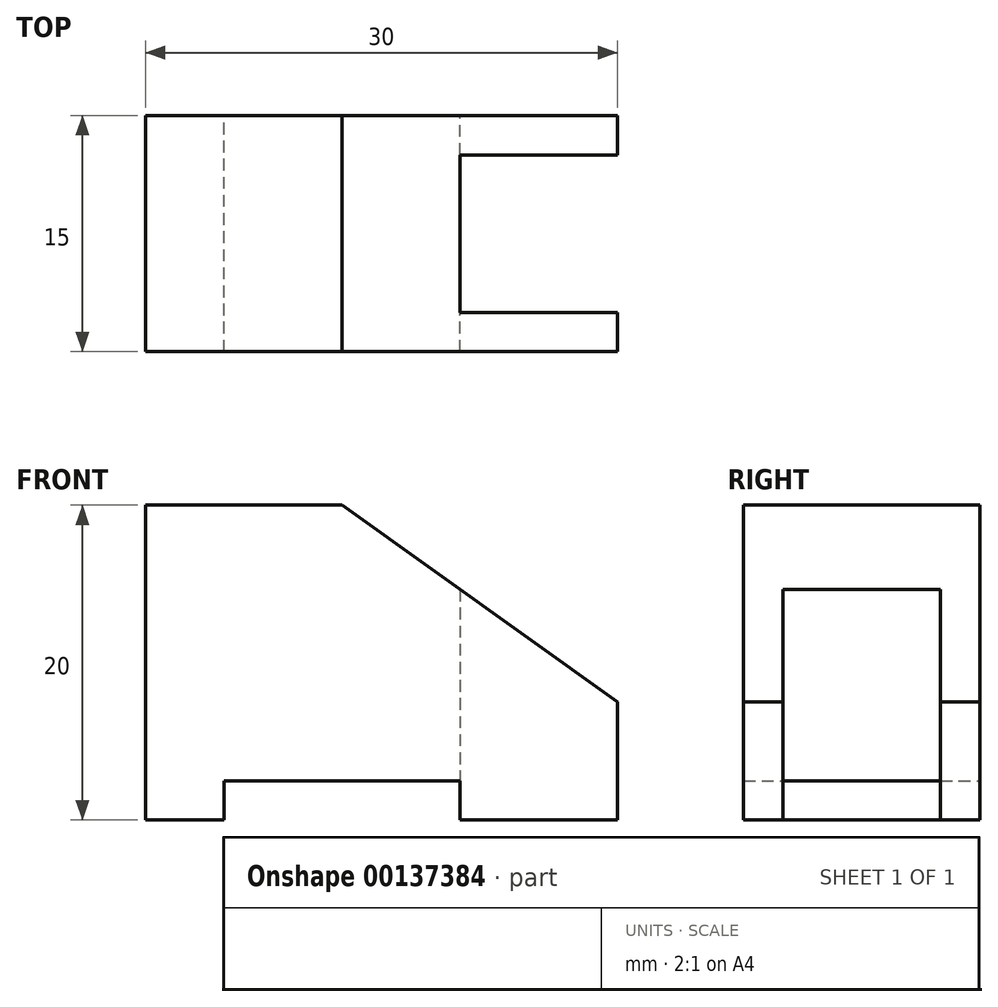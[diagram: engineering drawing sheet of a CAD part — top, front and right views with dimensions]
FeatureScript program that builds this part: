
annotation { "Feature Type Name" : "Feature", "Feature Type Description" : "" }
export const myFeature = defineFeature(function(context is Context, id is Id, definition is map)
    precondition{}
    {
        {
            var Q0;
            Q0=qCreatedBy(makeId("Front.planeOp"),FACE);
            var sketch = newSketch(context, id + "F0", { "sketchPlane" : qUnion([Q0])});
            skLineSegment(sketch, "E0", {"start": v(0, 0) * mm, "end": v(0, 20) * mm});
            skLineSegment(sketch, "E1", {"start": v(0, 20) * mm, "end": v(12.5, 20) * mm});
            skLineSegment(sketch, "E2", {"start": v(12.5, 20) * mm, "end": v(30, 7.5) * mm});
            skLineSegment(sketch, "E3", {"start": v(30, 7.5) * mm, "end": v(30, 0) * mm});
            skLineSegment(sketch, "E4", {"start": v(30, 0) * mm, "end": v(20, 0) * mm});
            skLineSegment(sketch, "E5", {"start": v(20, 0) * mm, "end": v(20, 2.5) * mm});
            skLineSegment(sketch, "E6", {"start": v(20, 2.5) * mm, "end": v(5, 2.5) * mm});
            skLineSegment(sketch, "E7", {"start": v(5, 2.5) * mm, "end": v(5, 0) * mm});
            skLineSegment(sketch, "E8", {"start": v(5, 0) * mm, "end": v(0, 0) * mm});
            skSolve(sketch);
        }
        {
            var Q0;
            Q0=qSketchRegion(id+"F0",true);
            extrude(context, id + "F1", {"entities" : qUnion([Q0]), "endBound" : BoundingType.SYMMETRIC, "depth" : 15 * mm});
        }
        {
            var Q0;
            Q0=qCreatedBy(makeId("Top.planeOp"),FACE);
            var sketch = newSketch(context, id + "F2", { "sketchPlane" : qUnion([Q0])});
            skLineSegment(sketch, "E9.bottom", {"start": v(30, -5) * mm, "end": v(20, -5) * mm});
            skLineSegment(sketch, "E9.top", {"start": v(30, 5) * mm, "end": v(20, 5) * mm});
            skLineSegment(sketch, "E9.left", {"start": v(30, -5) * mm, "end": v(30, 5) * mm});
            skLineSegment(sketch, "E9.right", {"start": v(20, -5) * mm, "end": v(20, 5) * mm});
            skSolve(sketch);
        }
        {
            var Q0;
            Q0=qSketchRegion(id+"F2",true);
            extrude(context, id + "F3", {"entities" : qUnion([Q0]), "operationType" : NewBodyOperationType.REMOVE, "depth" : 25 * mm});
        }
    });
